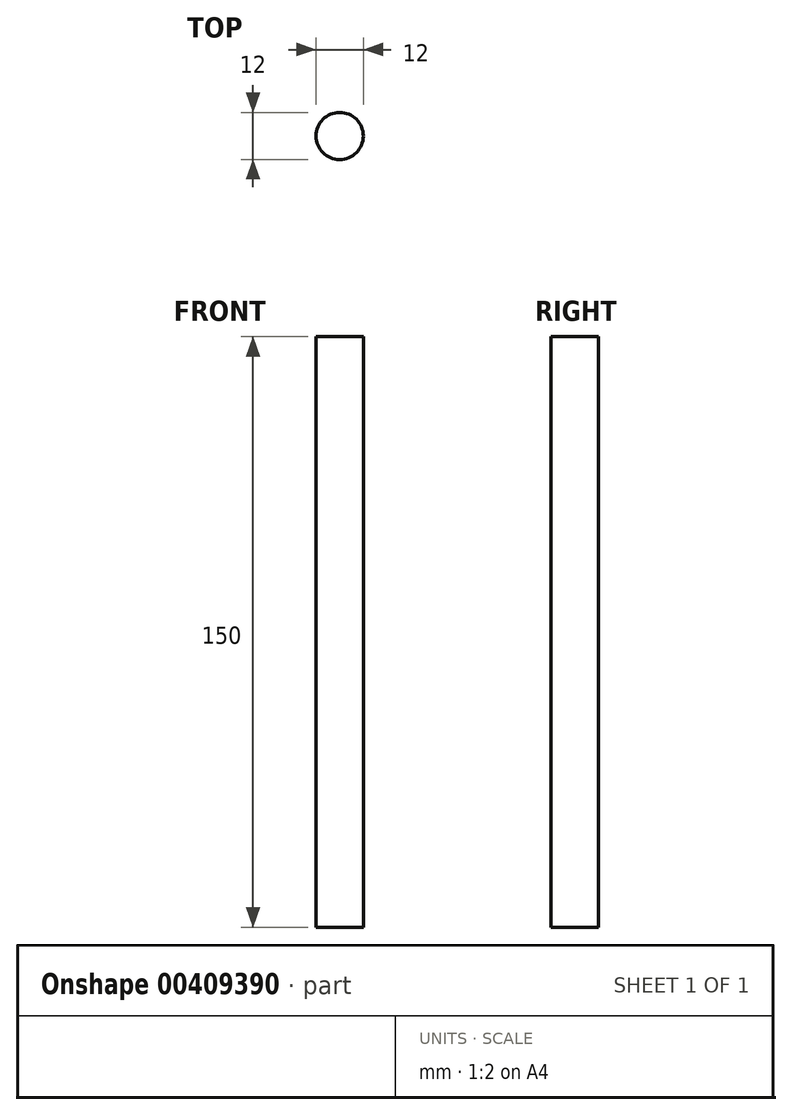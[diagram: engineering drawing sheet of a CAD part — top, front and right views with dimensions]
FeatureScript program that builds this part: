
annotation { "Feature Type Name" : "Feature", "Feature Type Description" : "" }
export const myFeature = defineFeature(function(context is Context, id is Id, definition is map)
    precondition{}
    {
        {
            var Q0;
            Q0=qCreatedBy(makeId("Top.planeOp"),FACE);
            var sketch = newSketch(context, id + "F0", { "sketchPlane" : qUnion([Q0])});
            skCircle(sketch, "E0", {"center": v(0, 0) * mm, "radius": 6 * mm});
            skSolve(sketch);
        }
        {
            var Q0;
            Q0=makeQuery(id+"F0.imprint","IMPRINT",FACE,{"disambiguationData":[TD([[makeQuery(id+"F0.imprint","IMPRINT",EDGE,{"derivedFrom":sQuery(id+"F0.wireOp",EDGE,"E0")}),1.0]])]});
            extrude(context, id + "F1", {"entities" : qUnion([Q0]), "depth" : 150 * mm});
        }
    });
